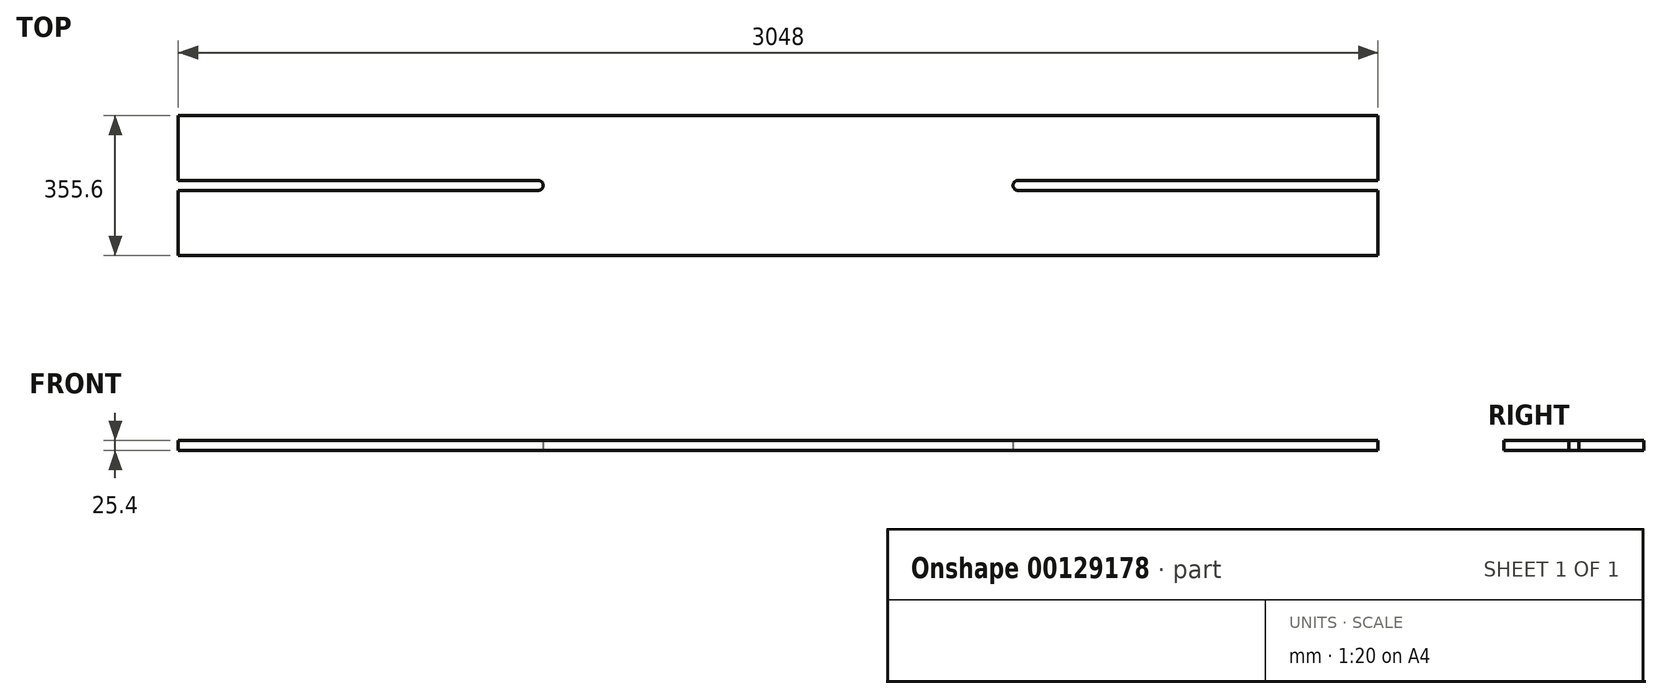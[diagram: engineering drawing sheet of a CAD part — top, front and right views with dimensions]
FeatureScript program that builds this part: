
annotation { "Feature Type Name" : "Feature", "Feature Type Description" : "" }
export const myFeature = defineFeature(function(context is Context, id is Id, definition is map)
    precondition{}
    {
        {
            var Q0;
            Q0=qCreatedBy(makeId("Top.planeOp"),FACE);
            var sketch = newSketch(context, id + "F0", { "sketchPlane" : qUnion([Q0])});
            skLineSegment(sketch, "E0.bottom", {"start": v(-1524, 177.8) * mm, "end": v(1524, 177.8) * mm});
            skLineSegment(sketch, "E0.top", {"start": v(-1524, -177.8) * mm, "end": v(1524, -177.8) * mm});
            skLineSegment(sketch, "E0.left", {"start": v(-1524, 177.8) * mm, "end": v(-1524, 12.7) * mm});
            skLineSegment(sketch, "E0.right", {"start": v(1524, 177.8) * mm, "end": v(1524, 12.7) * mm});
            skPoint(sketch, "E0.middle", {"position": v(0, 0) * mm});
            skLineSegment(sketch, "E1", {"start": v(-596.9, 0) * mm, "end": v(596.9, 0) * mm});
            skLineSegment(sketch, "E2", {"start": v(-609.6, -177.8) * mm, "end": v(-609.6, -12.7) * mm});
            skArc(sketch, "E3", {"start": v(-609.6, -12.7) * mm, "mid": v(-596.9, 0) * mm, "end": v(-609.6, 12.7) * mm});
            skLineSegment(sketch, "E4", {"start": v(-609.6, -12.7) * mm, "end": v(-1524, -12.7) * mm});
            skLineSegment(sketch, "E5", {"start": v(-609.6, 12.7) * mm, "end": v(-1524, 12.7) * mm});
            skPoint(sketch, "E6.orphan", {"position": v(-1524, 0) * mm});
            skLineSegment(sketch, "E7.trimOffspring", {"start": v(-609.6, 12.7) * mm, "end": v(-609.6, 177.8) * mm});
            skLineSegment(sketch, "E8.trimOffspring", {"start": v(-1524, -12.7) * mm, "end": v(-1524, -177.8) * mm});
            skLineSegment(sketch, "E9.MirrorCS", {"start": v(609.6, -12.7) * mm, "end": v(1524, -12.7) * mm});
            skLineSegment(sketch, "E10.MirrorCS", {"start": v(609.6, 12.7) * mm, "end": v(1524, 12.7) * mm});
            skArc(sketch, "E11.MirrorCS", {"start": v(609.6, -12.7) * mm, "mid": v(596.9, 0) * mm, "end": v(609.6, 12.7) * mm});
            skLineSegment(sketch, "E12.trimOffspring", {"start": v(1524, -12.7) * mm, "end": v(1524, -177.8) * mm});
            skPoint(sketch, "E13.orphan", {"position": v(1524, 0) * mm});
            skSolve(sketch);
        }
        {
            var Q0;
            Q0 = qSketchRegion(id + "F0", true);
            extrude(context, id + "F1", {"entities" : qUnion([Q0]), "depth" : 25.4 * mm});
        }
    });
